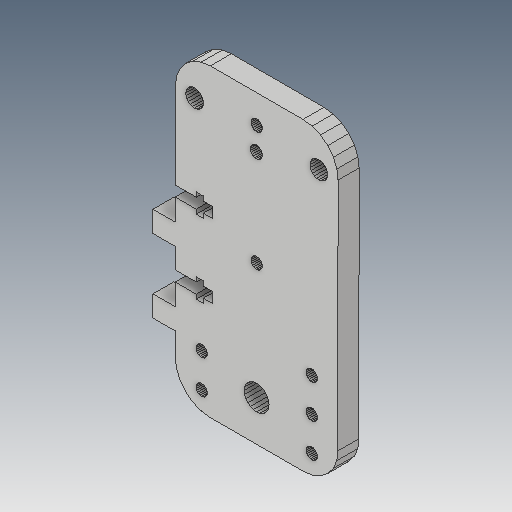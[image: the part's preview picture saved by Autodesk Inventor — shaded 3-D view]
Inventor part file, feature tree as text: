
AUTODESK INVENTOR PART (.ipt)
format: ipt  version: 2017 (Build 210142000, 142)  size: 502,784 bytes
history: native  units: mm
features: extrude x1, sketch x1
ambient origin geometry x8: Origin, YZ Plane, XZ Plane, XY Plane, X Axis, Y Axis, Z Axis, Center Point
bodies: Solid1 (feature_tree)
feature tree (2):
  extrude  "Extrusion1"  [1 undecoded]
  sketch  "Sketch1"  dims[d0=6.0mm d1=0.0mm]
note: 1 required parameter value undecoded (feature->parameter linkage not recoverable at this tier; creation-order binding heuristic only, values carry confidence <= 0.55)
